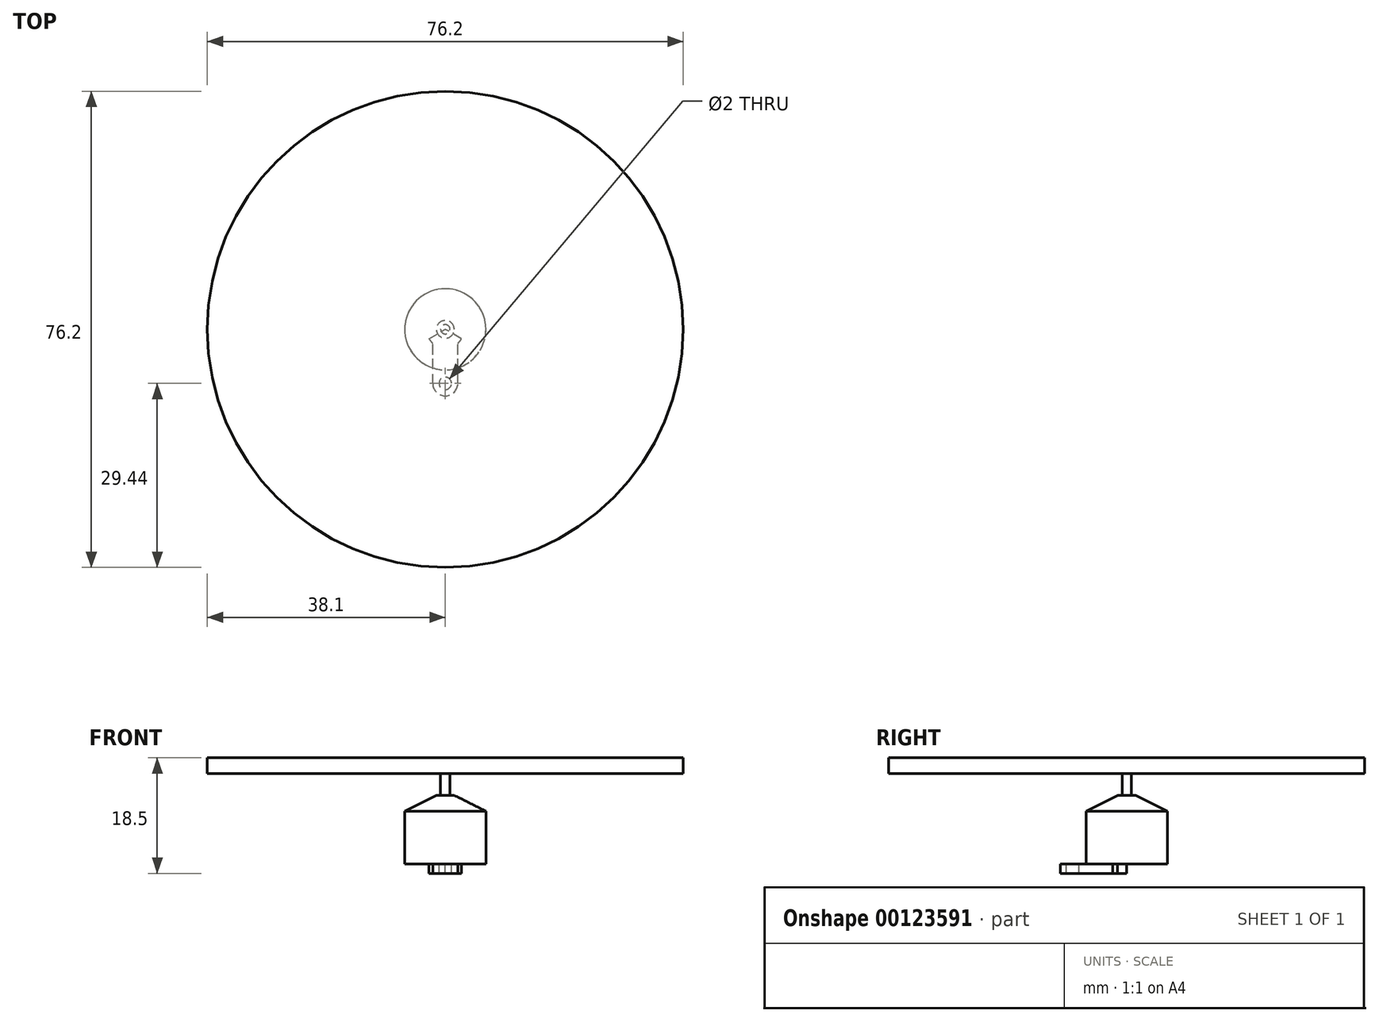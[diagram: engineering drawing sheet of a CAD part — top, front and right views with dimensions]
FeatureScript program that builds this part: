
annotation { "Feature Type Name" : "Feature", "Feature Type Description" : "" }
export const myFeature = defineFeature(function(context is Context, id is Id, definition is map)
    precondition{}
    {
        {
            var Q0;
            Q0=qCreatedBy(makeId("Top.planeOp"),FACE);
            var sketch = newSketch(context, id + "F0", { "sketchPlane" : qUnion([Q0])});
            skCircle(sketch, "E0", {"center": v(0, 0) * mm, "radius": 6.5 * mm});
            skSolve(sketch);
        }
        {
            var Q0;
            Q0=makeQuery(id+"F0.imprint","IMPRINT",FACE,{"disambiguationData":[TD([[makeQuery(id+"F0.imprint","IMPRINT",EDGE,{"derivedFrom":sQuery(id+"F0.wireOp",EDGE,"E0")}),1.0]])]});
            extrude(context, id + "F1", {"entities" : qUnion([Q0]), "depth" : 11 * mm});
        }
        {
            var Q0;
            Q0=makeQuery(id+"F1.opExtrude","CAP_FACE",FACE,{"disambiguationData":[OSD([sQuery(id+"F0.wireOp",EDGE,"E0")])],"isStart":false});
            var sketch = newSketch(context, id + "F2", { "sketchPlane" : qUnion([Q0])});
            skCircle(sketch, "E1", {"center": v(0, 0) * mm, "radius": 0.75 * mm});
            skSolve(sketch);
        }
        {
            var Q0;
            Q0 = qSketchRegion(id + "F2", true);
            extrude(context, id + "F3", {"entities" : qUnion([Q0]), "operationType" : NewBodyOperationType.ADD, "depth" : 6 * mm});
        }
        {
            var Q0;
            Q0=makeQuery(id+"F1.opExtrude","CAP_FACE",FACE,{"disambiguationData":[OSD([sQuery(id+"F0.wireOp",EDGE,"E0")])],"isStart":true});
            var sketch = newSketch(context, id + "F4", { "sketchPlane" : qUnion([Q0])});
            skCircle(sketch, "E2.cCircle", {"center": v(0, 0) * mm, "radius": 8.66 * mm, "construction": true});
            skLineSegment(sketch, "E2.0", {"start": v(0, 8.66) * mm, "end": v(7.5, -4.33) * mm, "construction": true});
            skLineSegment(sketch, "E2.1", {"start": v(7.5, -4.33) * mm, "end": v(-7.5, -4.33) * mm, "construction": true});
            skLineSegment(sketch, "E2.2", {"start": v(-7.5, -4.33) * mm, "end": v(0, 8.66) * mm, "construction": true});
            skLineSegment(sketch, "E3", {"start": v(0, 0) * mm, "end": v(-3.75, 2.17) * mm, "construction": true});
            skLineSegment(sketch, "E4", {"start": v(0, 0) * mm, "end": v(3.75, 2.17) * mm, "construction": true});
            skArc(sketch, "E5", {"start": v(-2, 8.66) * mm, "mid": v(0, 10.66) * mm, "end": v(2, 8.66) * mm});
            skLineSegment(sketch, "E6", {"start": v(-2, 8.66) * mm, "end": v(-2, 2.24) * mm});
            skLineSegment(sketch, "E7", {"start": v(2, 8.66) * mm, "end": v(2, 2.24) * mm});
            skArc(sketch, "E8", {"start": v(-2, 2.24) * mm, "mid": v(-2.33, 1.9) * mm, "end": v(-2.6, 1.5) * mm});
            skArc(sketch, "E9", {"start": v(2, 2.24) * mm, "mid": v(2.33, 1.9) * mm, "end": v(2.6, 1.5) * mm});
            skCircle(sketch, "E10", {"center": v(0, 8.66) * mm, "radius": 1 * mm});
            skLineSegment(sketch, "E11", {"start": v(-2.6, 1.5) * mm, "end": v(0, 0) * mm});
            skLineSegment(sketch, "E12", {"start": v(2.6, 1.5) * mm, "end": v(0, 0) * mm});
            skSolve(sketch);
        }
        {
            var Q0;
            Q0 = qSketchRegion(id + "F4", true);
            extrude(context, id + "F5", {"entities" : qUnion([Q0]), "operationType" : NewBodyOperationType.ADD, "depth" : 1.5 * mm});
        }
        {
            var Q0;
            Q0=makeQuery(id+"F1.opExtrude","CAP_EDGE",EDGE,{"disambiguationData":[OSD([sQuery(id+"F0.wireOp",EDGE,"E0")])],"isStart":false});
            chamfer(context, id + "F6", {"entities" : qUnion([Q0]), "chamferType" : ChamferType.TWO_OFFSETS, "width1" : 5.08 * mm, "oppositeDirection" : false, "width2" : 2.54 * mm, "tangentPropagation" : true});
        }
        {
            var Q0;
            Q0=makeQuery(id+"F3.opExtrude","CAP_FACE",FACE,{"disambiguationData":[OSD([sQuery(id+"F2.wireOp",EDGE,"E1")])],"isStart":false});
            var sketch = newSketch(context, id + "F7", { "sketchPlane" : qUnion([Q0])});
            skCircle(sketch, "E13", {"center": v(0, 0) * mm, "radius": 38.1 * mm});
            skSolve(sketch);
        }
        {
            var Q0;
            Q0 = qSketchRegion(id + "F7", true);
            extrude(context, id + "F8", {"entities" : qUnion([Q0]), "operationType" : NewBodyOperationType.ADD, "oppositeDirection" : true, "depth" : 2.54 * mm});
        }
    });
